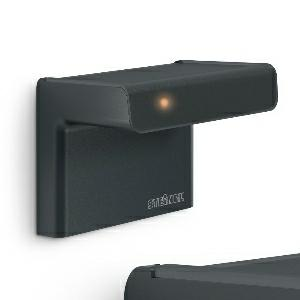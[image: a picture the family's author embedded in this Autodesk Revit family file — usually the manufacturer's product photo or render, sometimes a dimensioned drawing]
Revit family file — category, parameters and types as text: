
# Revit family: ihf_3d_007584
name_source: partatom
category: Elektroinstallationen
revit_build: Autodesk Revit 2016 (Build: 20190508_0715(x64)
units: mm (PartAtom-declared; Revit-internal decimal feet)

## family parameters
Basisbauteil = Fläche
Beim Laden mit Abzugskörper schneiden = Nein
Bemaßung runder Anschluss = Durchmesser verwenden
Beschriftungsausrichtung beibehalten = Nein
Gemeinsam genutzt = Nein
Raumberechnungspunkt = Nein
Teiletyp = Normal

## types (1)
- iHF 3D
    Apparent Load = 0 VA
    Beschreibung = Type: Motion detectors; Dimensions (L x W x H): 120 x 117 x 120 mm; Mains power supply: 120 – 250 V / 50 – 60 Hz; Power supply, detail: 500 VA max., 120 V; Sensor Technology: iHF (intelligent high-frequency technology); Application, place: Outdoors; Application, room: outdoors, front door, all round the building, terrace / balcony, courtyard & driveway; Installation site: wall; Installation: Surface wiring; HF-system: 5,8 GHz; Electronic scalability: Yes; Mechanical scalability: No; Mounting height: 1,80 – 2,00 m; Optimum mounting height: 1,8 m; Detection angle: 160 °; Sneak-by guard: Yes; Reach, detail: Detection zone adjustable on 3 axes; Reach, radial: r = 7 m (68 m²); Reach, tangential: r = 7 m (68 m²); Twilight setting TEACH: Yes; Twilight setting: 2 – 2000 lx; Time setting: 10 sec – 30 min; Switching output 1, resistive: 2000 W; Constant-lighting control: No; Basic light level function: No; Functions: Normal / test mode, Manual ON / ON-OFF; Settings via: Remote control, Potentiometers, Smart Remote; With remote control: No; Interconnection: Yes; Type of interconnection: Master/master; IP-rating: IP54; Material: Plastic; Ambient temperature: -20 – 50 °C; Colour: black; Colour, RAL: 9005; Manufacturer's Warranty: 5 years; Version: black; PU1, EAN: 4007841007584
    Height = 120 mm  [stored 0.393701 ft]
    Hersteller = Steinel
    Length = 120 mm  [stored 0.393701 ft]
    Maximum range = 6.431 m
    ModVariant = Nein
    Modell = 007584
    Mounting Type = Surface mounted
    Number of Poles = 1
    OnlyDefault = Ja
    Power Factor = 1
    Product Name = iHF 3D
    Product group = Sensor-switched indoor light
    ProductGroupID = 30
    Protection Class = Protection class II
    Protection Degree = IP 54
    RlxData = <blob elided: 156697 chars, md5=ccb743a0>
    Sensor characteristics = Semi circular 145°-300°
    Sensor type = HF
    SensorDataFile = <blob elided: 144225 chars, md5=4f57d913>
    Type of entry = Motion
    Typenbild = produkt1_007584.jpg
    Typenkommentare = Product without accessories
    URL = http://relux.com
    VarID = ---
    Voltage = 0 V
    Vorgabe-Ansicht = 1800 mm
    Weight = 0.00 kg
    Width = 117 mm

note: [stored X ft] marks values corroborated as IEEE doubles in the binary element streams (Revit-internal decimal feet)

## geometry (parser evidence)
native form markers: Blend x4, Sweep x17
no freeform markers — native parametric forms only
